# Revit family: Eurolan_Модуль вентиляторный потолочный
name_source: partatom
category: Устройства связи
units: mm (PartAtom-declared; Revit-internal decimal feet)

## family parameters
Всегда вертикально = Да
На основе рабочей плоскости = Нет
Общий = Нет
При загрузке вырезать с полостями = Нет
Размер круглого соединителя = Использовать диаметр
Сохранять ориентацию аннотаций = Нет
Тип детали = Нормальный
Точка расчета площади = Нет

## types (4) — shared parameters
ADSK_Единица измерения = шт
ADSK_Завод-изготовитель = Eurolan
ADSK_Количество = 1
ADSK_Наименование краткое = Модуль вентиляторный потолочный

## per-type parameters (varying)
| type | ADSK_Код изделия | ADSK_Масса | ADSK_Материал | ADSK_Наименование | Выбор_графики |
| 3 вентилятора_термореле_3 положения_черный | 60A-90-11-30BL | 2.4 | RAL9005 | Модуль вентиляторный потолочный, 3 вентилятора, термореле, 3 положения, черный | 3 вентилятора 3 положения : 3 вентилятора, термореле, 3 положения, черный |
| 3 вентилятора_термореле_3 положения_серый | 60A-90-11-30GY | 2.4 | RAL7035 | Модуль вентиляторный потолочный, 3 вентилятора, термореле, 3 положения, серый | 3 вентилятора 3 положения : 3 вентилятора, термореле, 3 положения, серый |
| 2 вентилятора_термореле_3 положения_черный | 60A-90-10-30BL | 1.8 | RAL9005 | Модуль вентиляторный потолочный, 2 вентилятора, термореле, 3 положения, черный | 2 вентилятора 3 положения : 2 вентилятора 3 положения черный |
| 2 вентилятора_термореле_3 положения_серый | 60A-90-10-30GY | 1.8 | RAL7035 | Модуль вентиляторный потолочный, 2 вентилятора, термореле, 3 положения, серый | 2 вентилятора 3 положения : 2 вентилятора 3 положения, серый |
